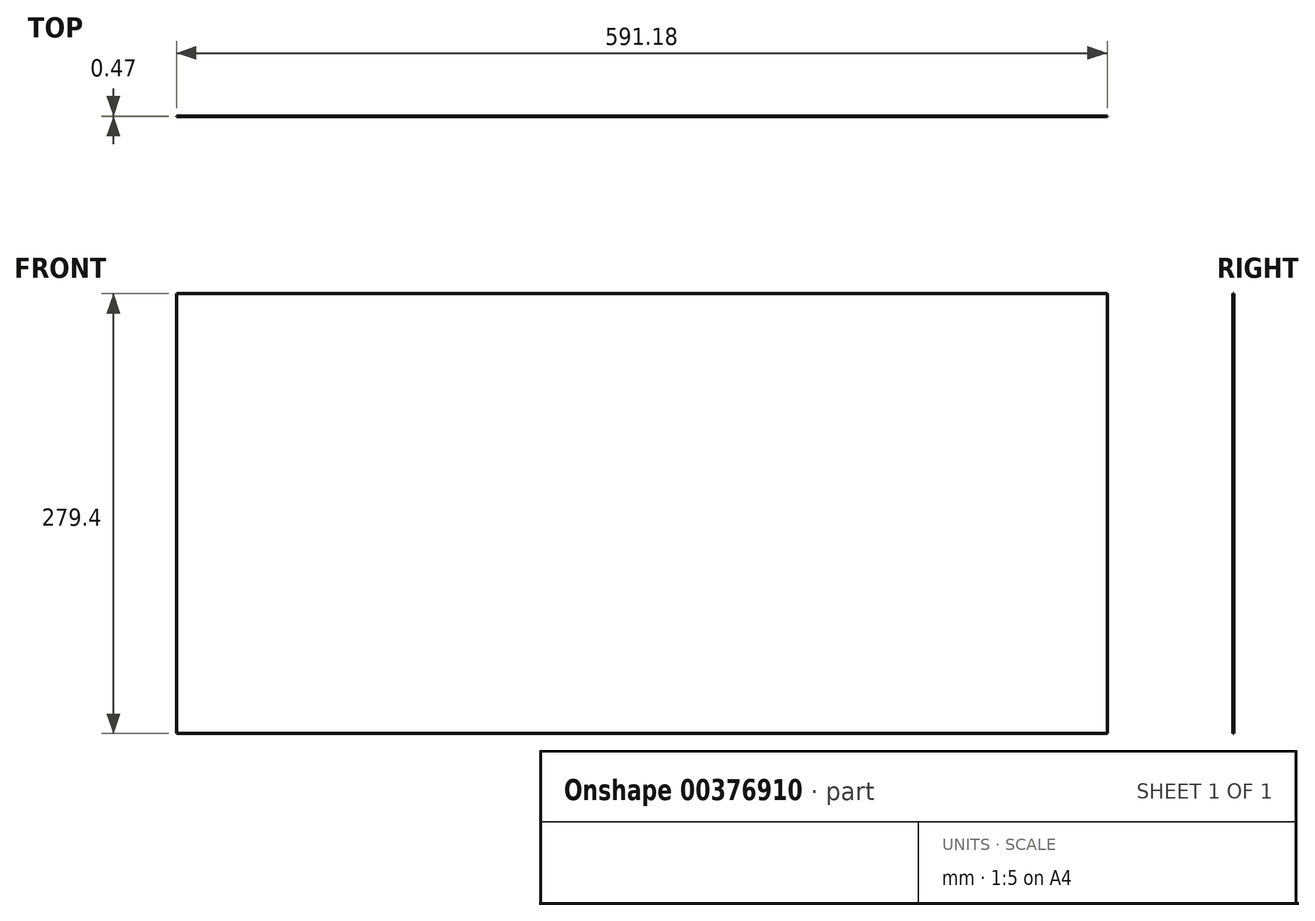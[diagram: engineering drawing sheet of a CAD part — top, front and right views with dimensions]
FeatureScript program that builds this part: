
annotation { "Feature Type Name" : "Feature", "Feature Type Description" : "" }
export const myFeature = defineFeature(function(context is Context, id is Id, definition is map)
    precondition{}
    {
        {
            var Q0;
            Q0=qCreatedBy(makeId("Front.planeOp"),FACE);
            var sketch = newSketch(context, id + "F0", { "sketchPlane" : qUnion([Q0])});
            skLineSegment(sketch, "E0.bottom", {"start": v(-301.62, -139.7) * mm, "end": v(301.63, -139.7) * mm});
            skLineSegment(sketch, "E0.top", {"start": v(-301.63, 139.7) * mm, "end": v(301.62, 139.7) * mm});
            skLineSegment(sketch, "E0.left", {"start": v(-301.62, -139.7) * mm, "end": v(-301.63, 139.7) * mm});
            skLineSegment(sketch, "E0.right", {"start": v(301.63, -139.7) * mm, "end": v(301.62, 139.7) * mm});
            skPoint(sketch, "E0.middle", {"position": v(0, 0) * mm});
            skSolve(sketch);
        }
        {
            assignVariable(context, id + "F1", {"name" : "material", "anyValue" : 0.47});
        }
        {
            var Q0;
            Q0=makeQuery(id+"F0.imprint","IMPRINT",FACE,{"disambiguationData":[TD([[makeQuery(id+"F0.imprint","IMPRINT",EDGE,{"derivedFrom":sQuery(id+"F0.wireOp",EDGE,"E0.bottom")}),1.0]])]});
            extrude(context, id + "F2", {"entities" : qUnion([Q0]), "depth" : (getVariable(context, 'material')) * mm});
        }
        {
            var Q0;
            Q0=makeQuery(id+"F2.opExtrude","SWEPT_FACE",FACE,{"disambiguationData":[OSD([sQuery(id+"F0.wireOp",EDGE,"E0.right")])]});
            extrude(context, id + "F3", {"entities" : qUnion([Q0]), "operationType" : NewBodyOperationType.REMOVE, "oppositeDirection" : true, "depth" : 6.03 * mm});
        }
        {
            var Q0;
            Q0=makeQuery(id+"F2.opExtrude","SWEPT_FACE",FACE,{"disambiguationData":[OSD([sQuery(id+"F0.wireOp",EDGE,"E0.left")])]});
            extrude(context, id + "F4", {"entities" : qUnion([Q0]), "operationType" : NewBodyOperationType.REMOVE, "oppositeDirection" : true, "depth" : 6.03 * mm});
        }
    });
